# Revit family: AV1010001_Grifería para Lavamanos 4 pulgadas Aluvia Palanca
name_source: partatom
category: Plumbing Fixtures
units: mm (PartAtom-declared; Revit-internal decimal feet)

## family parameters
Cut with Voids When Loaded = No
Host = Face
OmniClass Number = 23.31.11.00
OmniClass Title = Faucets
Part Type = Normal
Room Calculation Point = No
Round Connector Dimension = Use Diameter
Shared = No

## types (1)
- AV1010001_Grifería para Lavamanos 4 pulgadas Aluvia Palanca
    Alto = 104 mm
    Ancho = 218 mm
    Capacidad de flujo = 60 psi : 5,7 L/min.
    Default Elevation = 1219 mm
    Description = Aluvia integra líneas y formas como las de una erosión aluvial, su forma robusta está inspirada en el agua esculpiendo las rocas a través de los años dando paso a superficies más suaves, amigables y limpias evitando que haya acumulación de impurezas. El conjunto de manijas es el resultado de su diseño ergonómico, brindando un agarre cómodo sin importar el agua y el jabón.
    Garantía = 30 Años
    Longitud = 156 mm
    MATERIAL = Corona_Cromado
    Manufacturer = Corona
    Model = Grifería lavamanos 4 pulgadas palanca Aluvia
    Peso neto = 330 gr. - 0,72 lb.
    Presion maxima = 125 psi (862 Kpa).
    Presion minima = 20 psi (138 Kpa)
    Temperatura de uso = 5ºC a 71ºC.
    URL = https://www.corona.co
    Vida útil o desgaste (unidad) = 500.000 ciclos.

## geometry (parser evidence)
native form markers: Sweep x5
no freeform markers — native parametric forms only
